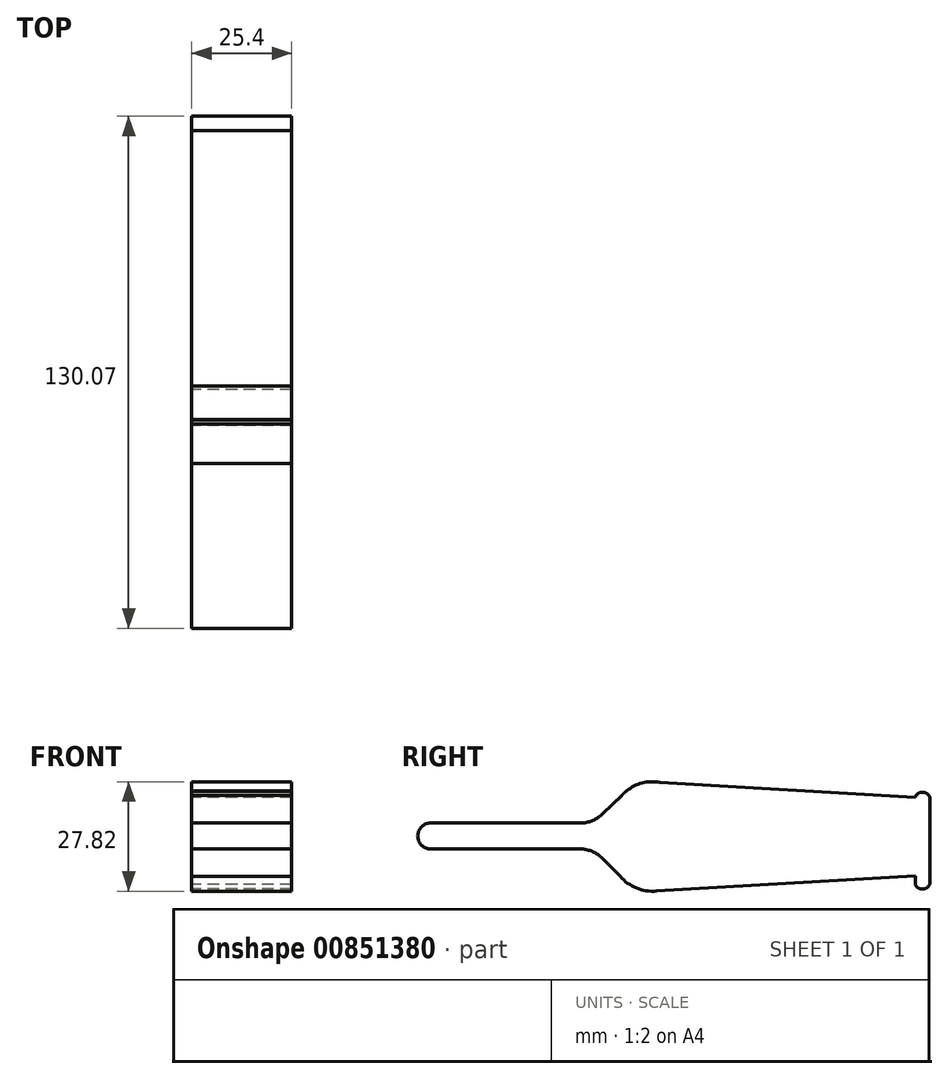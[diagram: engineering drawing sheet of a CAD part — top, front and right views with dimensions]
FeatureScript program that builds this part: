
annotation { "Feature Type Name" : "Feature", "Feature Type Description" : "" }
export const myFeature = defineFeature(function(context is Context, id is Id, definition is map)
    precondition{}
    {
        {
            var Q0;
            Q0=qCreatedBy(makeId("Right.planeOp"),FACE);
            var sketch = newSketch(context, id + "F0", { "sketchPlane" : qUnion([Q0])});
            skLineSegment(sketch, "E0", {"start": v(-119, 6.86) * mm, "end": v(-80.46, 6.86) * mm});
            skLineSegment(sketch, "E1", {"start": v(-119, 0.26) * mm, "end": v(-80.74, 0.26) * mm});
            skLineSegment(sketch, "E2", {"start": v(147.67, 0.26) * mm, "end": v(147.63, 6.86) * mm});
            skArc(sketch, "E3", {"start": v(-119, 6.86) * mm, "mid": v(-122.3, 3.56) * mm, "end": v(-119, 0.26) * mm});
            skPoint(sketch, "E4", {"position": v(-69.38, 3.64) * mm});
            skLineSegment(sketch, "E5.right", {"start": v(-81.1, 0.26) * mm, "end": v(-81.1, 6.86) * mm});
            skArc(sketch, "E6", {"start": v(-81.73, 6.86) * mm, "mid": v(-78.32, 7.32) * mm, "end": v(-75.39, 9.14) * mm});
            skArc(sketch, "E7", {"start": v(-75.39, -2.1) * mm, "mid": v(-78.17, -0.28) * mm, "end": v(-81.45, 0.26) * mm});
            skPoint(sketch, "E8", {"position": v(-81.1, 3.64) * mm});
            skLineSegment(sketch, "E9", {"start": v(-75.39, 9.14) * mm, "end": v(-69.26, 15.05) * mm});
            skLineSegment(sketch, "E10", {"start": v(-75.39, -2.1) * mm, "end": v(-69.63, -7.89) * mm});
            skArc(sketch, "E11", {"start": v(-70.85, -6.66) * mm, "mid": v(-66.72, -9.67) * mm, "end": v(-61.67, -10.42) * mm});
            skLineSegment(sketch, "E12.top", {"start": v(-61.67, 17.24) * mm, "end": v(-61.1, 17.24) * mm});
            skLineSegment(sketch, "E12.right", {"start": v(7.76, -8.69) * mm, "end": v(7.76, 13.44) * mm});
            skPoint(sketch, "E12.middle", {"position": v(-26.96, 3.41) * mm});
            skLineSegment(sketch, "E13.left", {"start": v(4.09, -8.69) * mm, "end": v(4.09, 13.44) * mm});
            skPoint(sketch, "E13.middle", {"position": v(7.76, 3.41) * mm});
            skLineSegment(sketch, "E14", {"start": v(-61.67, 17.24) * mm, "end": v(4.09, 13.44) * mm});
            skLineSegment(sketch, "E15", {"start": v(-61.67, -10.42) * mm, "end": v(4.09, -6.58) * mm});
            skArc(sketch, "E16", {"start": v(7.76, 13.44) * mm, "mid": v(5.92, 14.68) * mm, "end": v(4.09, 13.44) * mm});
            skArc(sketch, "E17", {"start": v(7.33, -10.42) * mm, "mid": v(7.28, -10.5) * mm, "end": v(7.24, -10.57) * mm});
            skPoint(sketch, "E18.orphan", {"position": v(7.76, -8.69) * mm});
            skArc(sketch, "E19", {"start": v(4.09, -8.69) * mm, "mid": v(5.92, -9.91) * mm, "end": v(7.76, -8.69) * mm});
            skLineSegment(sketch, "E20.trimOffspring", {"start": v(-80.46, 6.86) * mm, "end": v(-119, 6.86) * mm});
            skLineSegment(sketch, "E21.trimOffspring", {"start": v(-69.75, -7.78) * mm, "end": v(-69.76, -7.78) * mm});
            skPoint(sketch, "E22.orphan", {"position": v(-57.66, -7.78) * mm});
            skLineSegment(sketch, "E23.trimOffspring", {"start": v(-69.23, 15.05) * mm, "end": v(-69.26, 15.05) * mm});
            skArc(sketch, "E24.trimOffspring", {"start": v(-60.78, 17.2) * mm, "mid": v(-66.03, 16.8) * mm, "end": v(-70.43, 13.93) * mm});
            skPoint(sketch, "E5.left.end.orphan", {"position": v(-57.66, 15.05) * mm});
            skPoint(sketch, "E25.orphan", {"position": v(4.09, 15.51) * mm});
            skPoint(sketch, "E26.trimOffspring.end.orphan", {"position": v(7.76, 17.24) * mm});
            skPoint(sketch, "E27.orphan", {"position": v(11.43, 15.51) * mm});
            skPoint(sketch, "E28.orphan", {"position": v(11.43, -8.69) * mm});
            skPoint(sketch, "E29.orphan", {"position": v(7.76, -10.42) * mm});
            skLineSegment(sketch, "E30", {"start": v(-59.23, 17.1) * mm, "end": v(-59.23, -10.28) * mm});
            skLineSegment(sketch, "E31", {"start": v(-59.23, 3.41) * mm, "end": v(4.09, 3.41) * mm});
            skLineSegment(sketch, "E32", {"start": v(-104.37, 6.86) * mm, "end": v(-104.37, 0.26) * mm});
            skLineSegment(sketch, "E33", {"start": v(-63.1, 17.35) * mm, "end": v(-63.1, -10.45) * mm});
            skSolve(sketch);
        }
        {
            var Q0;
            Q0 = qSketchRegion(id + "F0", true);
            extrude(context, id + "F1", {"entities" : qUnion([Q0]), "depth" : 25.4 * mm, "offsetDistance" : 25.4 * mm});
        }
    });
